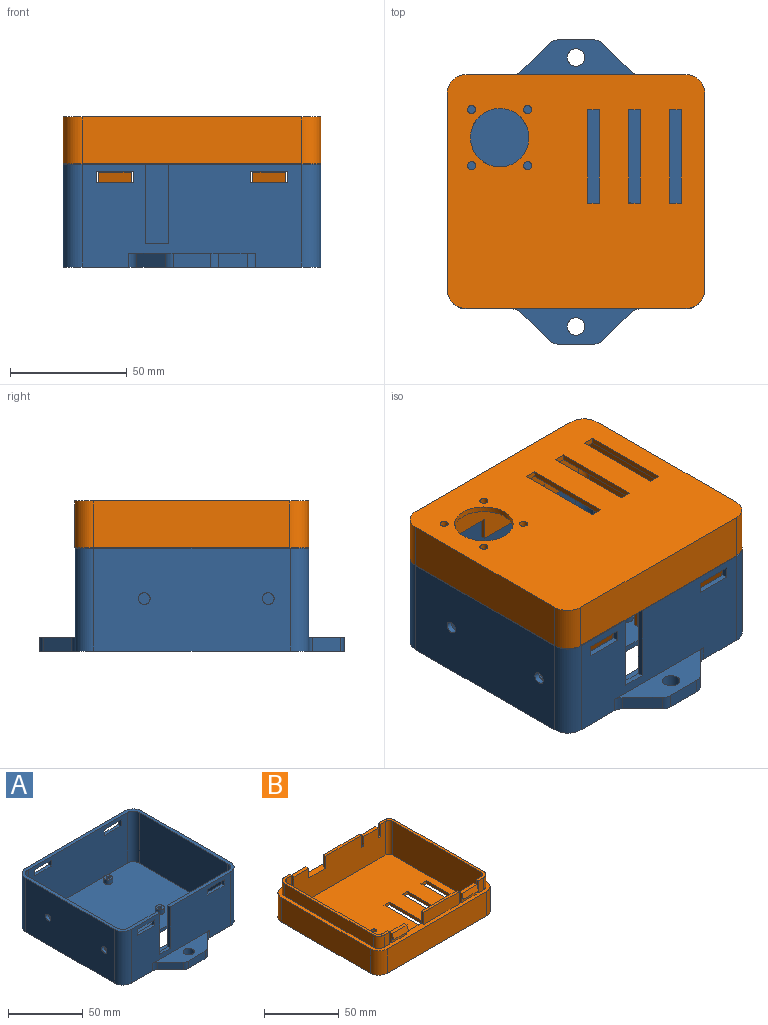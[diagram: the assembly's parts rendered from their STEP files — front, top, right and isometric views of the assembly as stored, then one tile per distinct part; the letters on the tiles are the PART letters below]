
ASSEMBLY  parts=2 mates=1
PART A: 86 faces, bbox 110x130x44 mm
  f0: plane 94x44mm, normal (0,-1,0), area 3317.5mm2, adj f9,f10,f13,f14,f58,f59,f62,f75
  f1: plane 94x41.6mm, normal (0,1,0), area 3416.8mm2, adj f8,f10,f19,f20,f75,f76,f77,f78
  f2: plane 94x44mm, normal (0,1,0), area 3657.5mm2, adj f9,f10,f15,f16,f53,f63,f64,f67
  f3: plane 94x41.6mm, normal (0,-1,0), area 3756.8mm2, adj f8,f10,f21,f22,f67,f68,f69,f70
  f4: cylinder r=1.38mm len=4.4mm, axis (0,0,1), area 38mm2, adj f30,f47
  f5: cylinder r=1.38mm len=4.4mm, axis (0,0,1), area 38mm2, adj f28,f45
  f6: cylinder r=1.38mm len=4.4mm, axis (0,0,1), area 38mm2, adj f26,f43
  f7: cylinder r=1.38mm len=4.4mm, axis (0,0,1), area 38mm2, adj f24,f41
  f8: plane 105.2x95.2mm, normal (0,0,1), area 9146.5mm2, adj f1,f3,f17,f18,f19,f20,f21,f22
  f9: plane 130x110mm, normal (0,0,-1), area 11099.6mm2, adj f0,f2,f11,f12,f13,f14,f15,f16
  f10: plane 110x100mm, normal (0,0,1), area 932.9mm2, adj f0,f1,f2,f3,f11,f12,f13,f14
  f11: plane 84x44mm, normal (-1,0,0), area 3656.7mm2, adj f9,f10,f13,f16,f31,f32
  f12: plane 84x44mm, normal (1,0,0), area 3696mm2, adj f9,f10,f14,f15
  f13: cylinder r=8mm len=44mm, axis (0,0,1), area 552.9mm2, adj f0,f9,f10,f11
  f14: cylinder r=8mm len=44mm, axis (0,0,-1), area 552.9mm2, adj f0,f9,f10,f12
  f15: cylinder r=8mm len=44mm, axis (0,0,1), area 552.9mm2, adj f2,f9,f10,f12
  f16: cylinder r=8mm len=44mm, axis (0,0,-1), area 552.9mm2, adj f2,f9,f10,f11
  f17: plane 84x41.6mm, normal (1,0,0), area 3455.1mm2, adj f8,f10,f19,f22,f31,f32
  f18: plane 84x41.6mm, normal (-1,0,0), area 3494.4mm2, adj f8,f10,f20,f21
  f19: cylinder r=5.6mm len=41.6mm, axis (0,0,1), area 365.9mm2, adj f1,f8,f10,f17
  f20: cylinder r=5.6mm len=41.6mm, axis (0,0,-1), area 365.9mm2, adj f1,f8,f10,f18
  f21: cylinder r=5.6mm len=41.6mm, axis (0,0,1), area 365.9mm2, adj f3,f8,f10,f18
  f22: cylinder r=5.6mm len=41.6mm, axis (0,0,-1), area 365.9mm2, adj f3,f8,f10,f17
  f23: cylinder r=3mm len=6mm, axis (0,0,-1), area 67.9mm2, adj f8,f24
  f24: plane 6x6mm, normal (0,0,1), area 22.3mm2, adj f7,f23
  f25: cylinder r=3mm len=6mm, axis (0,0,-1), area 67.9mm2, adj f8,f26
  f26: plane 6x6mm, normal (0,0,1), area 22.3mm2, adj f6,f25
  f27: cylinder r=3mm len=6mm, axis (0,0,-1), area 67.9mm2, adj f8,f28
  f28: plane 6x6mm, normal (0,0,1), area 22.3mm2, adj f5,f27
  f29: cylinder r=3mm len=6mm, axis (0,0,-1), area 67.9mm2, adj f8,f30
  f30: plane 6x6mm, normal (0,0,1), area 22.3mm2, adj f4,f29
  f31: cylinder r=2.5mm len=5mm, axis (1,0,0), area 37.7mm2, adj f11,f17
  f32: cylinder r=2.5mm len=5mm, axis (1,0,0), area 37.7mm2, adj f11,f17
  f33: plane 40x2.4mm, normal (0,-1,0), area 96mm2, adj f8,f9,f37,f40
  f34: plane 5x2.4mm, normal (1,0,0), area 12mm2, adj f8,f9,f37,f38
  f35: plane 40x2.4mm, normal (0,1,0), area 96mm2, adj f8,f9,f38,f39
  f36: plane 5x2.4mm, normal (-1,0,0), area 12mm2, adj f8,f9,f39,f40
  f37: cylinder r=5mm len=5mm, axis (0,0,1), area 18.8mm2, adj f8,f9,f33,f34
  f38: cylinder r=5mm len=5mm, axis (0,0,-1), area 18.8mm2, adj f8,f9,f34,f35
  f39: cylinder r=5mm len=5mm, axis (0,0,1), area 18.8mm2, adj f8,f9,f35,f36
  f40: cylinder r=5mm len=5mm, axis (0,0,-1), area 18.8mm2, adj f8,f9,f33,f36
  f41: plane 5x5mm, normal (0,0,-1), area 13.7mm2, adj f7,f42
  f42: cylinder r=2.5mm len=5mm, axis (0,0,-1), area 25.1mm2, adj f9,f41
  f43: plane 5x5mm, normal (0,0,-1), area 13.7mm2, adj f6,f44
  f44: cylinder r=2.5mm len=5mm, axis (0,0,-1), area 25.1mm2, adj f9,f43
  f45: plane 5x5mm, normal (0,0,-1), area 13.7mm2, adj f5,f46
  f46: cylinder r=2.5mm len=5mm, axis (0,0,-1), area 25.1mm2, adj f9,f45
  f47: plane 5x5mm, normal (0,0,-1), area 13.7mm2, adj f4,f48
  f48: cylinder r=2.5mm len=5mm, axis (0,0,-1), area 25.1mm2, adj f9,f47
  f49: plane 12.07x12.07mm, normal (-0.71,0.71,0), area 102.4mm2, adj f9,f53,f63,f66
  f50: plane 12.07x12.07mm, normal (0.71,0.71,0), area 102.4mm2, adj f9,f53,f64,f65
  f51: plane 15.86x6mm, normal (0,1,0), area 95.1mm2, adj f9,f53,f65,f66
  f52: cylinder r=3.75mm len=7.5mm, axis (0,0,-1), area 141.4mm2, adj f9,f53
  f53: plane 54.14x15mm, normal (0,0,1), area 480.8mm2, adj f2,f49,f50,f51,f52,f63,f64,f65
  f54: plane 12.07x12.07mm, normal (-0.71,-0.71,0), area 102.4mm2, adj f9,f58,f59,f60
  f55: plane 15.86x6mm, normal (0,-1,0), area 95.1mm2, adj f9,f58,f60,f61
  f56: cylinder r=3.75mm len=7.5mm, axis (0,0,-1), area 141.4mm2, adj f9,f58
  f57: plane 12.07x12.07mm, normal (0.71,-0.71,0), area 102.4mm2, adj f9,f58,f61,f62
  f58: plane 54.14x15mm, normal (0,0,1), area 480.8mm2, adj f0,f54,f55,f56,f57,f59,f60,f61
  f59: cylinder r=5mm len=6mm, axis (0,0,1), area 23.6mm2, adj f0,f9,f54,f58
  f60: cylinder r=5mm len=6mm, axis (0,0,-1), area 23.6mm2, adj f9,f54,f55,f58
  f61: cylinder r=5mm len=6mm, axis (0,0,-1), area 23.6mm2, adj f9,f55,f57,f58
  f62: cylinder r=5mm len=6mm, axis (0,0,1), area 23.6mm2, adj f0,f9,f57,f58
  f63: cylinder r=5mm len=6mm, axis (0,0,1), area 23.6mm2, adj f2,f9,f49,f53
  f64: cylinder r=5mm len=6mm, axis (0,0,1), area 23.6mm2, adj f2,f9,f50,f53
  f65: cylinder r=5mm len=6mm, axis (0,0,-1), area 23.6mm2, adj f9,f50,f51,f53
  f66: cylinder r=5mm len=6mm, axis (0,0,-1), area 23.6mm2, adj f9,f49,f51,f53
  f67: plane 4.8x2.4mm, normal (-1,0,0), area 11.5mm2, adj f2,f3,f68,f70
  f68: plane 16x2.4mm, normal (0,0,1), area 38.4mm2, adj f2,f3,f67,f69
  f69: plane 4.8x2.4mm, normal (1,0,0), area 11.5mm2, adj f2,f3,f68,f70
  f70: plane 16x2.4mm, normal (0,0,-1), area 38.4mm2, adj f2,f3,f67,f69
  f71: plane 4.8x2.4mm, normal (-1,0,0), area 11.5mm2, adj f2,f3,f72,f74
  f72: plane 16x2.4mm, normal (0,0,1), area 38.4mm2, adj f2,f3,f71,f73
  f73: plane 4.8x2.4mm, normal (1,0,0), area 11.5mm2, adj f2,f3,f72,f74
  f74: plane 16x2.4mm, normal (0,0,-1), area 38.4mm2, adj f2,f3,f71,f73
  f75: plane 16x2.4mm, normal (0,0,-1), area 38.4mm2, adj f0,f1,f76,f78
  f76: plane 4.8x2.4mm, normal (1,0,0), area 11.5mm2, adj f0,f1,f75,f77
  f77: plane 16x2.4mm, normal (0,0,1), area 38.4mm2, adj f0,f1,f76,f78
  f78: plane 4.8x2.4mm, normal (-1,0,0), area 11.5mm2, adj f0,f1,f75,f77
  f79: plane 16x2.4mm, normal (0,0,-1), area 38.4mm2, adj f0,f1,f80,f82
  f80: plane 4.8x2.4mm, normal (1,0,0), area 11.5mm2, adj f0,f1,f79,f81
  f81: plane 16x2.4mm, normal (0,0,1), area 38.4mm2, adj f0,f1,f80,f82
  f82: plane 4.8x2.4mm, normal (-1,0,0), area 11.5mm2, adj f0,f1,f79,f81
  f83: plane 34x2.4mm, normal (1,0,0), area 81.6mm2, adj f0,f1,f10,f84
  f84: plane 10x2.4mm, normal (0,0,1), area 24mm2, adj f0,f1,f83,f85
  f85: plane 34x2.4mm, normal (-1,0,0), area 81.6mm2, adj f0,f1,f10,f84
PART B: 84 faces, bbox 110x100x30 mm
  f0: plane 94x27.6mm, normal (0,1,0), area 2318.4mm2, adj f5,f9,f10,f11,f12,f23,f25,f26
  f1: plane 94x27.6mm, normal (0,-1,0), area 2318.4mm2, adj f5,f6,f7,f8,f23,f24,f25,f27
  f2: plane 34x10mm, normal (0,1,0), area 340mm2, adj f24,f27,f53,f83
  f3: plane 34x10mm, normal (0,-1,0), area 340mm2, adj f26,f27,f54,f82
  f4: plane 110x100mm, normal (0,0,-1), area 9815.7mm2, adj f28,f29,f30,f31,f32,f33,f34,f35
  f5: plane 100.4x90.4mm, normal (0,0,1), area 7938mm2, adj f0,f1,f44,f45,f46,f47,f48,f49
  f6: plane 8x4mm, normal (1,0,0), area 21.8mm2, adj f1,f14,f19,f27,f58,f63
  f7: plane 8x4mm, normal (1,0,0), area 21.8mm2, adj f1,f13,f21,f27,f57,f64
  f8: plane 8x4mm, normal (-1,0,0), area 21.8mm2, adj f1,f14,f19,f27,f58,f63
  f9: plane 8x4mm, normal (-1,0,0), area 21.8mm2, adj f0,f15,f18,f27,f59,f62
  f10: plane 8x4mm, normal (1,0,0), area 21.8mm2, adj f0,f15,f18,f27,f59,f62
  f11: plane 8x4mm, normal (1,0,0), area 21.8mm2, adj f0,f16,f17,f27,f60,f61
  f12: plane 8x4mm, normal (-1,0,0), area 21.8mm2, adj f0,f16,f17,f27,f60,f61
  f13: plane 14x4.4mm, normal (0,0.95,0.3), area 64.5mm2, adj f7,f51,f57,f64
  f14: plane 14x4.4mm, normal (0,0.95,0.3), area 64.5mm2, adj f6,f8,f58,f63
  f15: plane 14x4.4mm, normal (0,-0.95,0.3), area 64.5mm2, adj f9,f10,f59,f62
  f16: plane 14x4.4mm, normal (0,-0.95,0.3), area 64.5mm2, adj f11,f12,f60,f61
  f17: plane 14x3.6mm, normal (0,-1,0), area 50.4mm2, adj f11,f12,f27,f60
  f18: plane 14x3.6mm, normal (0,-1,0), area 50.4mm2, adj f9,f10,f27,f59
  f19: plane 14x3.6mm, normal (0,1,0), area 50.4mm2, adj f6,f8,f27,f58
  f20: plane 10x5mm, normal (0,1,0), area 50mm2, adj f25,f27,f37,f52
  f21: plane 14x3.6mm, normal (0,1,0), area 50.4mm2, adj f7,f27,f51,f57
  f22: plane 10x5mm, normal (0,-1,0), area 50mm2, adj f25,f27,f43,f55
  f23: plane 94.4x10.2mm, normal (0,0,1), area 214.4mm2, adj f0,f1,f38,f39,f40,f41,f42,f47
  f24: plane 34x2mm, normal (0,0,1), area 68mm2, adj f1,f2,f53,f83
  f25: plane 94.4x10.2mm, normal (0,0,1), area 214.4mm2, adj f0,f1,f20,f22,f36,f37,f43,f44
  f26: plane 34x2mm, normal (0,0,1), area 68mm2, adj f0,f3,f54,f82
  f27: plane 110x100mm, normal (0,0,1), area 1200.9mm2, adj f0,f1,f2,f3,f6,f7,f8,f9
  f28: plane 84x20mm, normal (-1,0,0), area 1680mm2, adj f4,f27,f32,f35
  f29: plane 94x20mm, normal (0,-1,0), area 1880mm2, adj f4,f27,f32,f33
  f30: plane 84x20mm, normal (1,0,0), area 1680mm2, adj f4,f27,f33,f34
  f31: plane 94x20mm, normal (0,1,0), area 1880mm2, adj f4,f27,f34,f35
  f32: cylinder r=8mm len=20mm, axis (0,0,1), area 251.3mm2, adj f4,f27,f28,f29
  f33: cylinder r=8mm len=20mm, axis (0,0,-1), area 251.3mm2, adj f4,f27,f29,f30
  f34: cylinder r=8mm len=20mm, axis (0,0,1), area 251.3mm2, adj f4,f27,f30,f31
  f35: cylinder r=8mm len=20mm, axis (0,0,-1), area 251.3mm2, adj f4,f27,f28,f31
  f36: plane 84x10mm, normal (1,0,0), area 840mm2, adj f25,f27,f37,f43
  f37: cylinder r=5.2mm len=10mm, axis (0,0,-1), area 81.7mm2, adj f20,f25,f27,f36
  f38: plane 10x5mm, normal (0,1,0), area 50mm2, adj f23,f27,f39,f50
  f39: cylinder r=5.2mm len=10mm, axis (0,0,-1), area 81.7mm2, adj f23,f27,f38,f40
  f40: plane 84x10mm, normal (-1,0,0), area 840mm2, adj f23,f27,f39,f41
  f41: cylinder r=5.2mm len=10mm, axis (0,0,-1), area 81.7mm2, adj f23,f27,f40,f42
  f42: plane 10x5mm, normal (0,-1,0), area 50mm2, adj f23,f27,f41,f56
  f43: cylinder r=5.2mm len=10mm, axis (0,0,-1), area 81.7mm2, adj f22,f25,f27,f36
  f44: cylinder r=3.2mm len=27.6mm, axis (0,0,-1), area 138.7mm2, adj f0,f5,f25,f45
  f45: plane 84x27.6mm, normal (-1,0,0), area 2318.4mm2, adj f5,f25,f44,f46
  f46: cylinder r=3.2mm len=27.6mm, axis (0,0,1), area 138.7mm2, adj f1,f5,f25,f45
  f47: cylinder r=3.2mm len=27.6mm, axis (0,0,-1), area 138.7mm2, adj f1,f5,f23,f48
  f48: plane 84x27.6mm, normal (1,0,0), area 2318.4mm2, adj f5,f23,f47,f49
  f49: cylinder r=3.2mm len=27.6mm, axis (0,0,1), area 138.7mm2, adj f0,f5,f23,f48
  f50: plane 10x2mm, normal (1,0,0), area 20mm2, adj f1,f23,f27,f38
  f51: plane 8x4mm, normal (-1,0,0), area 21.8mm2, adj f1,f13,f21,f27,f57,f64
  f52: plane 10x2mm, normal (-1,0,0), area 20mm2, adj f1,f20,f25,f27
  f53: plane 10x2mm, normal (1,0,0), area 20mm2, adj f1,f2,f24,f27
  f54: plane 10x2mm, normal (1,0,0), area 20mm2, adj f0,f3,f26,f27
  f55: plane 10x2mm, normal (-1,0,0), area 20mm2, adj f0,f22,f25,f27
  f56: plane 10x2mm, normal (1,0,0), area 20mm2, adj f0,f23,f27,f42
  f57: plane 14x2mm, normal (0,0,-1), area 28mm2, adj f7,f13,f21,f51
  f58: plane 14x2mm, normal (0,0,-1), area 28mm2, adj f6,f8,f14,f19
  f59: plane 14x2mm, normal (0,0,-1), area 28mm2, adj f9,f10,f15,f18
  f60: plane 14x2mm, normal (0,0,-1), area 28mm2, adj f11,f12,f16,f17
  f61: plane 14x2.63mm, normal (0,0,1), area 36.8mm2, adj f0,f11,f12,f16
  f62: plane 14x2.63mm, normal (0,0,1), area 36.8mm2, adj f0,f9,f10,f15
  f63: plane 14x2.63mm, normal (0,0,1), area 36.7mm2, adj f1,f6,f8,f14
  f64: plane 14x2.63mm, normal (0,0,1), area 36.7mm2, adj f1,f7,f13,f51
  f65: cylinder r=1.75mm len=3.5mm, axis (0,0,-1), area 26.4mm2, adj f4,f5
  f66: cylinder r=1.75mm len=3.5mm, axis (0,0,-1), area 26.4mm2, adj f4,f5
  f67: cylinder r=1.75mm len=3.5mm, axis (0,0,-1), area 26.4mm2, adj f4,f5
  f68: cylinder r=1.75mm len=3.5mm, axis (0,0,-1), area 26.4mm2, adj f4,f5
  f69: cylinder r=12.5mm len=25mm, axis (0,0,-1), area 188.5mm2, adj f4,f5
  f70: plane 5x2.4mm, normal (0,1,0), area 12mm2, adj f4,f5,f71,f73
  f71: plane 40x2.4mm, normal (1,0,0), area 96mm2, adj f4,f5,f70,f72
  f72: plane 5x2.4mm, normal (0,-1,0), area 12mm2, adj f4,f5,f71,f73
  f73: plane 40x2.4mm, normal (-1,0,0), area 96mm2, adj f4,f5,f70,f72
  f74: plane 40x2.4mm, normal (1,0,0), area 96mm2, adj f4,f5,f75,f77
  f75: plane 5x2.4mm, normal (0,-1,0), area 12mm2, adj f4,f5,f74,f76
  f76: plane 40x2.4mm, normal (-1,0,0), area 96mm2, adj f4,f5,f75,f77
  f77: plane 5x2.4mm, normal (0,1,0), area 12mm2, adj f4,f5,f74,f76
  f78: plane 5x2.4mm, normal (0,1,0), area 12mm2, adj f4,f5,f79,f81
  f79: plane 40x2.4mm, normal (1,0,0), area 96mm2, adj f4,f5,f78,f80
  f80: plane 5x2.4mm, normal (0,-1,0), area 12mm2, adj f4,f5,f79,f81
  f81: plane 40x2.4mm, normal (-1,0,0), area 96mm2, adj f4,f5,f78,f80
  f82: plane 10x2mm, normal (-1,0,0), area 20mm2, adj f0,f3,f26,f27
  f83: plane 10x2mm, normal (-1,0,0), area 20mm2, adj f1,f2,f24,f27
PLACE A t=(-7.69,-7.12,1.34)mm fixed
PLACE B rot(axis=(1,0,0),180deg) t=(-7.69,93,65.5)mm
MATE planar B.f28 <-> A.f11  axis (-1,0,0) through (-7.69,43,55.5)mm
